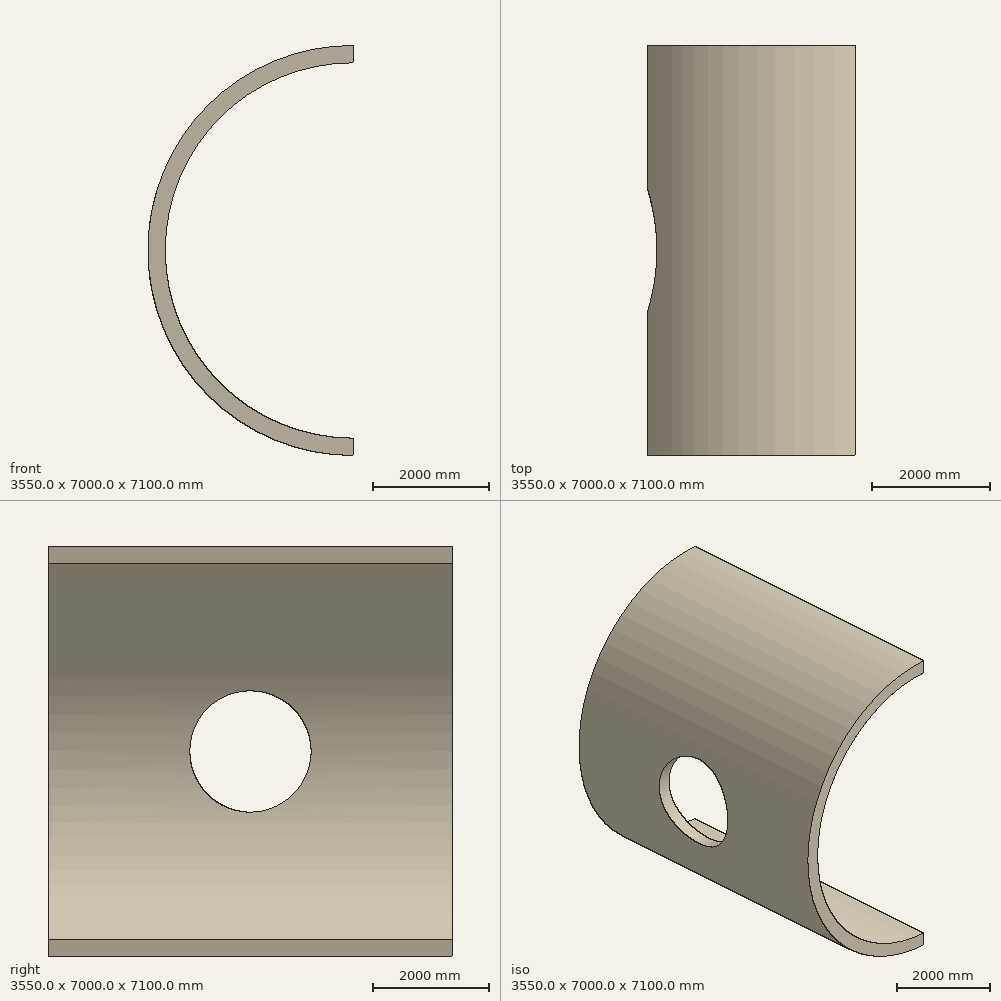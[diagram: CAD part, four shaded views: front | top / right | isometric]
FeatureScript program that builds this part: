
annotation { "Feature Type Name" : "Feature", "Feature Type Description" : "" }
export const myFeature = defineFeature(function(context is Context, id is Id, definition is map)
    precondition{}
    {
        {
            var Q0;
            Q0=qCreatedBy(makeId("Front.planeOp"),FACE);
            var sketch = newSketch(context, id + "F0", { "sketchPlane" : qUnion([Q0])});
            skArc(sketch, "E0", {"start": v(0, 3250) * mm, "mid": v(-3250, 0) * mm, "end": v(0, -3250) * mm});
            skArc(sketch, "E1", {"start": v(0, 3550) * mm, "mid": v(-3550, 0) * mm, "end": v(0, -3550) * mm});
            skLineSegment(sketch, "E2", {"start": v(0, 3550) * mm, "end": v(0, -3550) * mm});
            skSolve(sketch);
        }
        {
            var Q0;
            {var subQ0=sQuery(id+"F0.wireOp",EDGE,"E0");Q0=makeQuery(id+"F0.imprint","IMPRINT",FACE,{"disambiguationData":[TD([[makeQuery(id+"F0.imprint","IMPRINT",EDGE,{"derivedFrom":subQ0}),-1.0]])]});}
            extrude(context, id + "F1", {"entities" : qUnion([Q0]), "depth" : 7000 * mm, "offsetDistance" : 25 * mm});
        }
        {
            var Q0;
            Q0=qCreatedBy(makeId("Right.planeOp"),FACE);
            var sketch = newSketch(context, id + "F2", { "sketchPlane" : qUnion([Q0])});
            skCircle(sketch, "E3", {"center": v(-100000, 0) * mm, "radius": 1050 * mm});
            skSolve(sketch);
        }
        {
            var Q0;
            Q0 = qSketchRegion(id + "F2", true);
            extrude(context, id + "F3", {"entities" : qUnion([Q0]), "operationType" : NewBodyOperationType.REMOVE, "oppositeDirection" : true, "depth" : 10000 * mm, "offsetDistance" : 25 * mm});
        }
        {
            var Q0;
            Q0=qCreatedBy(makeId("Right.planeOp"),FACE);
            var sketch = newSketch(context, id + "F4", { "sketchPlane" : qUnion([Q0])});
            skCircle(sketch, "E4", {"center": v(-3500, 0) * mm, "radius": 1050 * mm});
            skSolve(sketch);
        }
        {
            var Q0;
            Q0 = qSketchRegion(id + "F4", true);
            extrude(context, id + "F5", {"entities" : qUnion([Q0]), "operationType" : NewBodyOperationType.REMOVE, "oppositeDirection" : true, "depth" : 10000 * mm, "offsetDistance" : 25 * mm});
        }
    });
